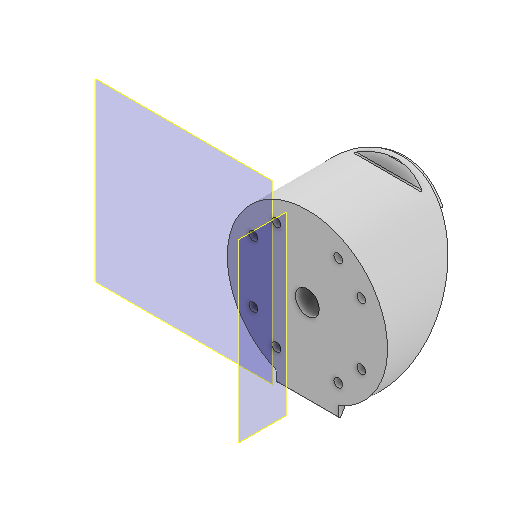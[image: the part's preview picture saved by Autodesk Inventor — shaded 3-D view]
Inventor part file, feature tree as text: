
AUTODESK INVENTOR PART (.ipt)
format: ipt  version: 2022 (Build 260153000, 153)  size: 219,136 bytes
history: native  units: in
note: dims shown in document units (in); Inventor stores cm internally (conversion verified against a paired STEP export)
features: reference x9, sketch x5, other x5, extrude x4, projected_geometry x4, plane x3, hole x1
ambient origin geometry x8: Origin, YZ Plane, XZ Plane, XY Plane, X Axis, Y Axis, Z Axis, Center Point
bodies: Solid1 (feature_tree)
feature tree (31):
  plane  "Work Plane1"
  plane  "Arbeitsebene5"
  extrude  "Extrusion1"  Depth=0.315in
  extrude  "Extrusion13"  Depth=0.0394in TaperAngle=0.0deg
  plane  "Arbeitsebene6"
  extrude  "Extrusion14"  Depth=0.0197in TaperAngle=0.0deg
  extrude  "Extrusion15"  TaperAngle=90.0deg  [1 undecoded]
  hole  "Bohrung3"  [1 undecoded]
  sketch  "Sketch1"  dims[d0=0.1969in d1=0.0in d2=0.315in]
  reference  "Reference1"
  reference  "Reference2"
  reference  "Reference3"
  reference  "Reference4"
  reference  "Reference5"
  reference  "Reference6"
  reference  "Reference7"
  reference  "Reference8"
  sketch  "Skizze17"  dims[d65=0.0079in d66=0.0394in d67=0.0in]
  reference  "Referenz30"
  projected_geometry  "Projizierte Kontur2"
  sketch  "Skizze18"  dims[d68=0.0197in d69=0.7874in d70=0.0in]
  projected_geometry  "Projizierte Kontur3"
  projected_geometry  "Projizierte Kontur4"
  sketch  "Skizze19"  dims[d71=135.0deg d72=90.0deg]
  projected_geometry  "Projizierte Kontur5"
  sketch  "Skizze20"  dims[d73=0.0197in d74=0.0in d75=0.0in d76=0.1102in d77=0.2362in d78=0.2559in d79=0.1181in d80=90.0deg d81=0.5512in d82=0.8108in]
  other  "Assembly1"
  other  "Assembly_MANATEE_V0_Manatee_middle2_v0_18:1"
  other  "Spectroscope_v0.iam"
  other  "00_Grating_1000linesPerMM:1"
  other  "Matchboxscope_bottom_v0:1"
note: 2 required parameter values undecoded (feature->parameter linkage not recoverable at this tier; creation-order binding heuristic only, values carry confidence <= 0.55)
